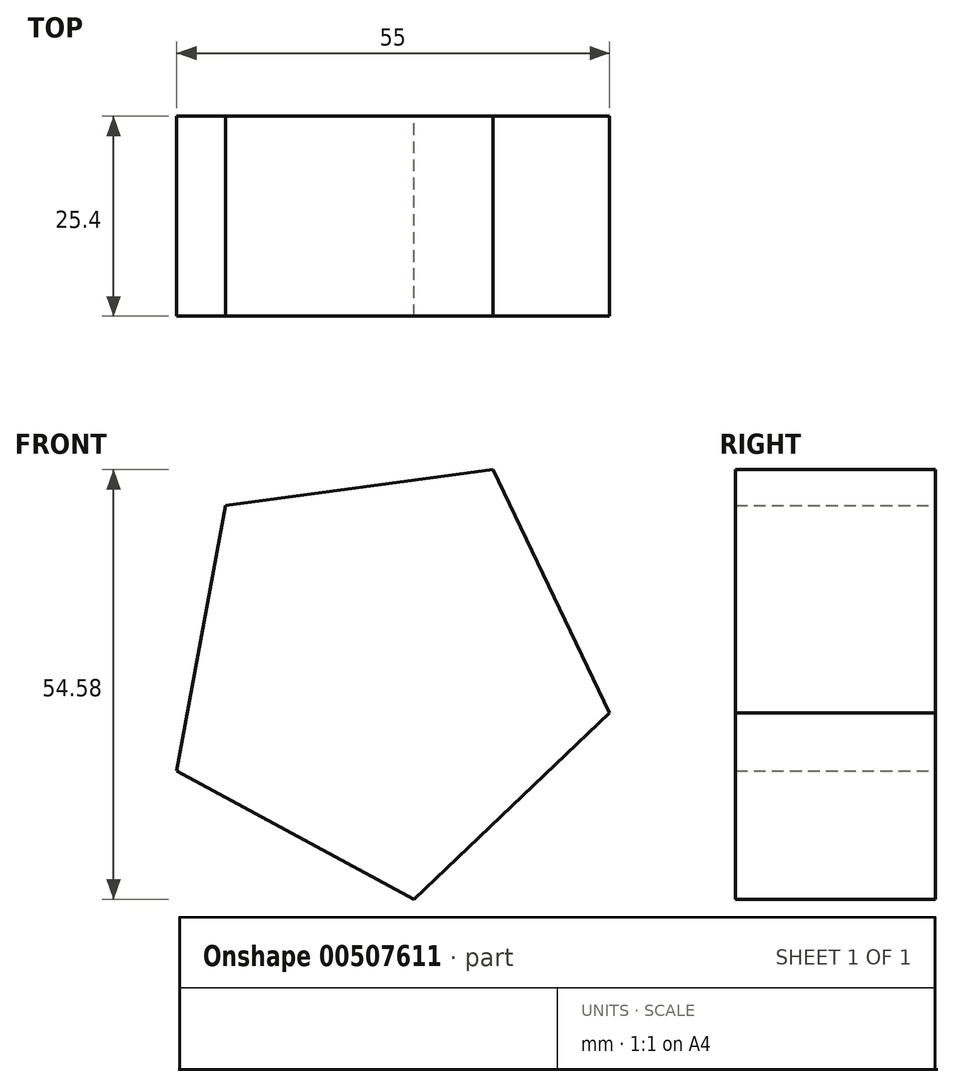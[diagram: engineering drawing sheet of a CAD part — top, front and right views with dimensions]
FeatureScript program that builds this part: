
annotation { "Feature Type Name" : "Feature", "Feature Type Description" : "" }
export const myFeature = defineFeature(function(context is Context, id is Id, definition is map)
    precondition{}
    {
        {
            var Q0;
            Q0=qCreatedBy(makeId("Front.planeOp"),FACE);
            var sketch = newSketch(context, id + "F0", { "sketchPlane" : qUnion([Q0])});
            skCircle(sketch, "E0.cCircle", {"center": v(0, 0) * mm, "radius": 29.17 * mm, "construction": true});
            skLineSegment(sketch, "E0.0", {"start": v(-20.11, 21.13) * mm, "end": v(13.88, 25.66) * mm});
            skLineSegment(sketch, "E0.1", {"start": v(13.88, 25.66) * mm, "end": v(28.7, -5.27) * mm});
            skLineSegment(sketch, "E0.2", {"start": v(28.7, -5.27) * mm, "end": v(3.85, -28.92) * mm});
            skLineSegment(sketch, "E0.3", {"start": v(3.85, -28.92) * mm, "end": v(-26.31, -12.6) * mm});
            skLineSegment(sketch, "E0.4", {"start": v(-26.31, -12.6) * mm, "end": v(-20.11, 21.13) * mm});
            skSolve(sketch);
        }
        {
            var Q0;
            Q0=makeQuery(id+"F0.imprint","IMPRINT",FACE,{"disambiguationData":[TD([[makeQuery(id+"F0.imprint","IMPRINT",EDGE,{"derivedFrom":sQuery(id+"F0.wireOp",EDGE,"E0.0")}),-1.0]])]});
            extrude(context, id + "F1", {"entities" : qUnion([Q0]), "depth" : 25.4 * mm});
        }
    });
